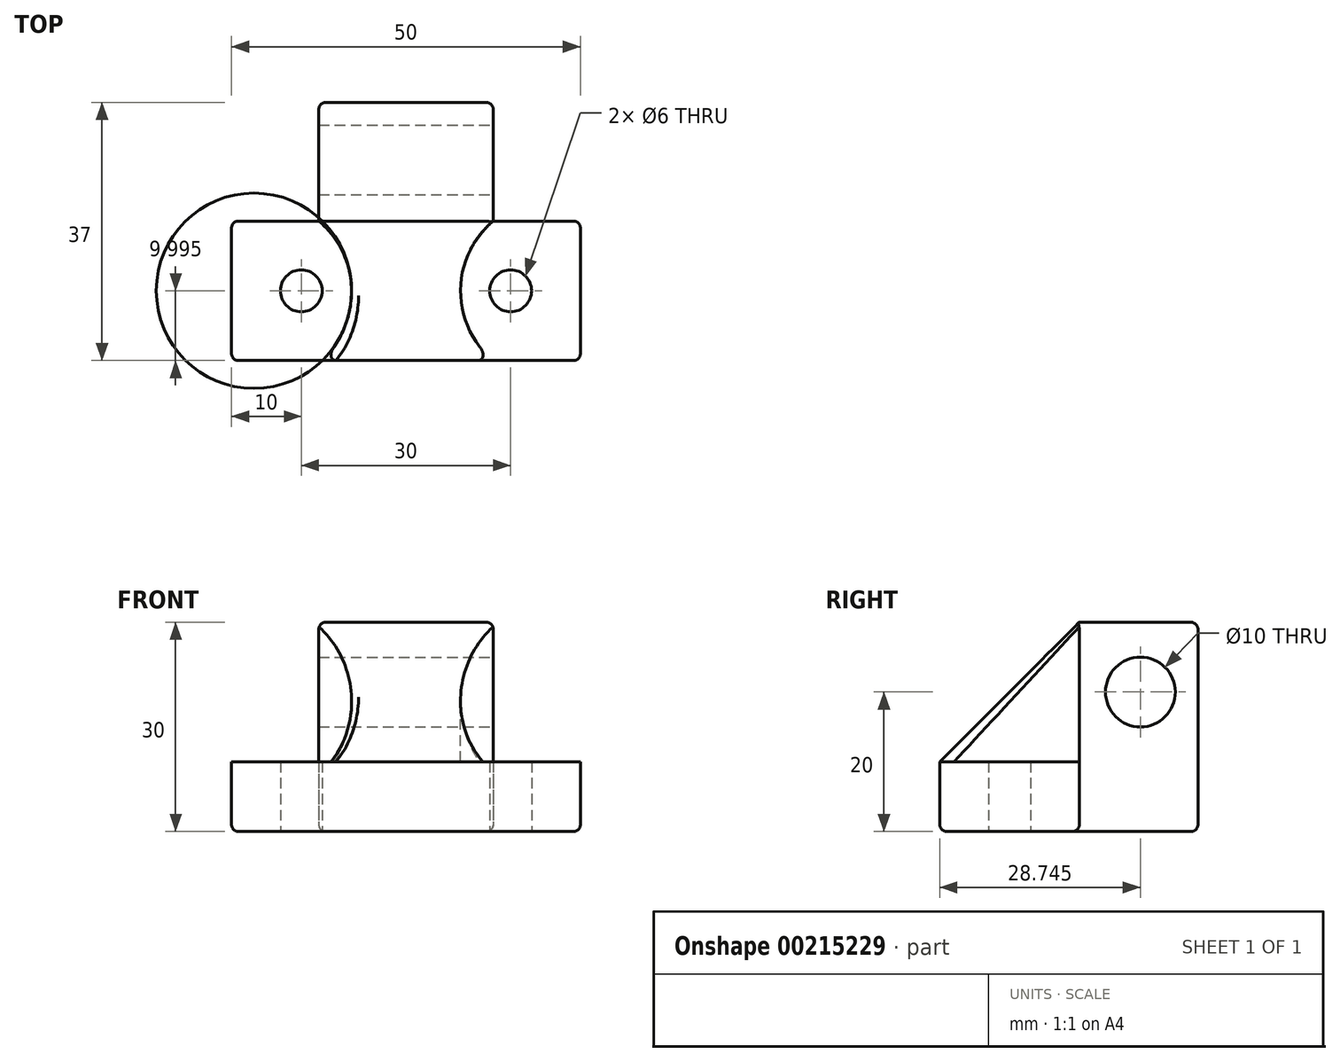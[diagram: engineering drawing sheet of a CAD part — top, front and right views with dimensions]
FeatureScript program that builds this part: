
annotation { "Feature Type Name" : "Feature", "Feature Type Description" : "" }
export const myFeature = defineFeature(function(context is Context, id is Id, definition is map)
    precondition{}
    {
        {
            var Q0;
            Q0=qCreatedBy(makeId("Top.planeOp"),FACE);
            var sketch = newSketch(context, id + "F0", { "sketchPlane" : qUnion([Q0])});
            skLineSegment(sketch, "E0.bottom", {"start": v(-9.5, 23.5) * mm, "end": v(15.5, 23.5) * mm});
            skLineSegment(sketch, "E0.top", {"start": v(-22, -13.5) * mm, "end": v(28, -13.5) * mm});
            skLineSegment(sketch, "E0.left", {"start": v(-22, 6.5) * mm, "end": v(-22, -13.5) * mm});
            skLineSegment(sketch, "E0.right", {"start": v(28, 6.5) * mm, "end": v(28, -13.5) * mm});
            skLineSegment(sketch, "E1", {"start": v(-9.5, 6.5) * mm, "end": v(-9.5, 23.5) * mm, "construction": true});
            skLineSegment(sketch, "E2", {"start": v(15.5, 23.5) * mm, "end": v(15.5, 6.5) * mm, "construction": true});
            skLineSegment(sketch, "E3", {"start": v(15.5, 23.5) * mm, "end": v(15.5, 6.5) * mm});
            skLineSegment(sketch, "E4", {"start": v(15.5, 6.5) * mm, "end": v(28, 6.5) * mm});
            skLineSegment(sketch, "E5", {"start": v(-9.5, 23.5) * mm, "end": v(-9.5, 6.5) * mm});
            skLineSegment(sketch, "E6.trimOffspring", {"start": v(15.5, 6.5) * mm, "end": v(28, 6.5) * mm, "construction": true});
            skLineSegment(sketch, "E7", {"start": v(3, 23.5) * mm, "end": v(3, -13.5) * mm, "construction": true});
            skPoint(sketch, "E8.trimOffspring.end.orphan", {"position": v(23, 23.5) * mm});
            skLineSegment(sketch, "E9", {"start": v(-22, -3.5) * mm, "end": v(28, -3.5) * mm, "construction": true});
            skLineSegment(sketch, "E10", {"start": v(18, -13.5) * mm, "end": v(18, 6.5) * mm, "construction": true});
            skLineSegment(sketch, "E11", {"start": v(18, 6.5) * mm, "end": v(15.5, 6.5) * mm});
            skLineSegment(sketch, "E12", {"start": v(-22, 6.5) * mm, "end": v(-9.5, 6.5) * mm});
            skLineSegment(sketch, "E13", {"start": v(-12, 6.5) * mm, "end": v(-12, -13.5) * mm, "construction": true});
            skCircle(sketch, "E14", {"center": v(-12, -3.5) * mm, "radius": 3 * mm});
            skCircle(sketch, "E15", {"center": v(18, -3.5) * mm, "radius": 3 * mm});
            skSolve(sketch);
        }
        {
            var Q0;
            Q0=makeQuery(id+"F0.imprint","IMPRINT",FACE,{"disambiguationData":[TD([[makeQuery(id+"F0.imprint","IMPRINT",EDGE,{"derivedFrom":sQuery(id+"F0.wireOp",EDGE,"E0.bottom")}),-1.0]])]});
            extrude(context, id + "F1", {"entities" : qUnion([Q0]), "depth" : 30 * mm});
        }
        {
            var Q0;
            Q0=makeQuery(id+"F1.opExtrude","CAP_FACE",FACE,{"disambiguationData":[OSD([sQuery(id+"F0.wireOp",EDGE,"E0.bottom"),sQuery(id+"F0.wireOp",EDGE,"E0.top"),sQuery(id+"F0.wireOp",EDGE,"E0.left"),sQuery(id+"F0.wireOp",EDGE,"E0.right"),sQuery(id+"F0.wireOp",EDGE,"E3"),sQuery(id+"F0.wireOp",EDGE,"E4"),sQuery(id+"F0.wireOp",EDGE,"E5"),sQuery(id+"F0.wireOp",EDGE,"E11"),sQuery(id+"F0.wireOp",EDGE,"E12"),sQuery(id+"F0.wireOp",EDGE,"E14"),sQuery(id+"F0.wireOp",EDGE,"E15")])],"isStart":false});
            var sketch = newSketch(context, id + "F2", { "sketchPlane" : qUnion([Q0])});
            skLineSegment(sketch, "E16.bottom", {"start": v(15.5, 6.5) * mm, "end": v(28, 6.5) * mm});
            skLineSegment(sketch, "E16.right", {"start": v(28, 6.5) * mm, "end": v(28, -13.5) * mm});
            skLineSegment(sketch, "E17.bottom", {"start": v(-22, 6.5) * mm, "end": v(-9.5, 6.5) * mm});
            skLineSegment(sketch, "E17.left", {"start": v(-22, 6.5) * mm, "end": v(-22, -13.5) * mm});
            skArc(sketch, "E18", {"start": v(-4.8, -3.5) * mm, "mid": v(-6.03, 2.02) * mm, "end": v(-9.5, 6.5) * mm});
            skArc(sketch, "E19", {"start": v(-9, -13.5) * mm, "mid": v(-5.89, -8.93) * mm, "end": v(-4.8, -3.5) * mm});
            skArc(sketch, "E20", {"start": v(15.5, 6.5) * mm, "mid": v(12.04, 2.02) * mm, "end": v(10.8, -3.5) * mm});
            skArc(sketch, "E21", {"start": v(10.8, -3.5) * mm, "mid": v(12.04, -9.03) * mm, "end": v(15.5, -13.5) * mm});
            skPoint(sketch, "E22.trimOffspring.end.orphan", {"position": v(28, -3.5) * mm});
            skPoint(sketch, "E23.start.orphan", {"position": v(-22, -3.5) * mm});
            skSolve(sketch);
        }
        {
            var Q0;
            Q0=makeQuery(id+"F2.imprint","IMPRINT",FACE,{"disambiguationData":[TD([[makeQuery(id+"F2.imprint","IMPRINT",EDGE,{"derivedFrom":sQuery(id+"F2.wireOp",EDGE,"E17.bottom")}),-1.0]])]});
            var Q1;
            Q1=makeQuery(id+"F2.imprint","IMPRINT",FACE,{"disambiguationData":[TD([[makeQuery(id+"F2.imprint","IMPRINT",EDGE,{"derivedFrom":sQuery(id+"F2.wireOp",EDGE,"E16.bottom")}),-1.0]])]});
            extrude(context, id + "F3", {"entities" : qUnion([Q0, Q1]), "operationType" : NewBodyOperationType.REMOVE, "oppositeDirection" : true, "depth" : 20 * mm});
        }
        {
            var Q0;
            Q0=makeQuery(id+"F1.opExtrude","SWEPT_FACE",FACE,{"disambiguationData":[OSD([sQuery(id+"F0.wireOp",EDGE,"E0.right")])]});
            var sketch = newSketch(context, id + "F4", { "sketchPlane" : qUnion([Q0])});
            skLineSegment(sketch, "E24.top", {"start": v(-13.5, 30) * mm, "end": v(6.5, 30) * mm});
            skLineSegment(sketch, "E24.left", {"start": v(-13.5, 10) * mm, "end": v(-13.5, 30) * mm});
            skLineSegment(sketch, "E25", {"start": v(-13.5, 10) * mm, "end": v(6.5, 30) * mm});
            skSolve(sketch);
        }
        {
            var Q0;
            Q0=makeQuery(id+"F4.imprint","IMPRINT",FACE,{"disambiguationData":[TD([[makeQuery(id+"F4.imprint","IMPRINT",EDGE,{"derivedFrom":sQuery(id+"F4.wireOp",EDGE,"E24.top")}),-1.0]])]});
            extrude(context, id + "F5", {"entities" : qUnion([Q0]), "operationType" : NewBodyOperationType.REMOVE, "oppositeDirection" : true, "depth" : 50 * mm});
        }
        {
            var Q0;
            Q0=makeQuery(id+"F1.opExtrude","SWEPT_FACE",FACE,{"disambiguationData":[OSD([sQuery(id+"F0.wireOp",EDGE,"E3")])]});
            var sketch = newSketch(context, id + "F6", { "sketchPlane" : qUnion([Q0])});
            skCircle(sketch, "E26", {"center": v(15.25, 20) * mm, "radius": 5 * mm});
            skPoint(sketch, "E27.trimOffspring.end.orphan", {"position": v(13.5, 0) * mm});
            skPoint(sketch, "E28.orphan", {"position": v(6.5, 20) * mm});
            skSolve(sketch);
        }
        {
            var Q0;
            Q0=makeQuery(id+"F6.imprint","IMPRINT",FACE,{"disambiguationData":[TD([[makeQuery(id+"F6.imprint","IMPRINT",EDGE,{"derivedFrom":sQuery(id+"F6.wireOp",EDGE,"E26")}),1.0]])]});
            extrude(context, id + "F7", {"entities" : qUnion([Q0]), "operationType" : NewBodyOperationType.REMOVE, "oppositeDirection" : true, "depth" : 25 * mm});
        }
        {
            var Q0;
            Q0=makeQuery(id+"F1.opExtrude","CAP_EDGE",EDGE,{"disambiguationData":[OSD([sQuery(id+"F0.wireOp",EDGE,"E0.bottom")])],"isStart":false});
            var Q1;
            Q1=makeQuery(id+"F1.opExtrude","CAP_EDGE",EDGE,{"disambiguationData":[OSD([sQuery(id+"F0.wireOp",EDGE,"E3")])],"isStart":false});
            var Q2;
            Q2=makeQuery(id+"F1.opExtrude","CAP_EDGE",EDGE,{"disambiguationData":[OSD([sQuery(id+"F0.wireOp",EDGE,"E5")])],"isStart":false});
            var Q3;
            Q3=makeQuery(id+"F3.boolean.opBoolean","COPY",EDGE,{"derivedFrom":makeQuery(id+"F3.opExtrude","CAP_EDGE",EDGE,{"disambiguationData":[OSD([sQuery(id+"F2.wireOp",EDGE,"E16.right")])],"isStart":false})});
            var Q4;
            Q4=makeQuery(id+"F3.boolean.opBoolean","COPY",EDGE,{"derivedFrom":makeQuery(id+"F3.opExtrude","CAP_EDGE",EDGE,{"disambiguationData":[OSD([sQuery(id+"F2.wireOp",EDGE,"E16.bottom")])],"isStart":false})});
            var Q5;
            {var subQ0=sQuery(id+"F0.wireOp",EDGE,"E0.top");var subQ1=makeQuery(id+"F1.opExtrude","CAP_EDGE",EDGE,{"disambiguationData":[OSD([subQ0])],"isStart":false});Q5=makeQuery(id+"F3.boolean.opBoolean","COPY",EDGE,{"derivedFrom":makeQuery(id+"F3.opExtrude","CAP_EDGE",EDGE,{"disambiguationData":[OSD([subQ0]),TDD([makeQuery(id+"F2.imprint","IMPRINT",EDGE,{"disambiguationData":[TD([[makeQuery(id+"F2.imprint","INTERSECT",VERTEX,{"derivedFrom":[subQ1,sQuery(id+"F2.wireOp",EDGE,"E16.right")]}),1.0]])],"derivedFrom":subQ1})])],"isStart":false})});}
            var Q6;
            Q6=makeQuery(id+"F1.opExtrude","SWEPT_EDGE",EDGE,{"disambiguationData":[OSD([sQuery(id+"F0.wireOp",EDGE,"E0.top"),sQuery(id+"F0.wireOp",EDGE,"E0.right")])]});
            var Q7;
            Q7=makeQuery(id+"F1.opExtrude","CAP_EDGE",EDGE,{"disambiguationData":[OSD([sQuery(id+"F0.wireOp",EDGE,"E0.right")])],"isStart":true});
            var Q8;
            Q8=makeQuery(id+"F1.opExtrude","SWEPT_EDGE",EDGE,{"disambiguationData":[OSD([sQuery(id+"F0.wireOp",EDGE,"E0.right"),sQuery(id+"F0.wireOp",EDGE,"E4")])]});
            var Q9;
            Q9=makeQuery(id+"F1.opExtrude","CAP_EDGE",EDGE,{"disambiguationData":[OSD([sQuery(id+"F0.wireOp",EDGE,"E3")])],"isStart":true});
            var Q10;
            Q10=makeQuery(id+"F1.opExtrude","SWEPT_EDGE",EDGE,{"disambiguationData":[OSD([sQuery(id+"F0.wireOp",EDGE,"E0.bottom"),sQuery(id+"F0.wireOp",EDGE,"E3")])]});
            var Q11;
            Q11=makeQuery(id+"F1.opExtrude","CAP_EDGE",EDGE,{"disambiguationData":[OSD([sQuery(id+"F0.wireOp",EDGE,"E0.bottom")])],"isStart":true});
            var Q12;
            Q12=makeQuery(id+"F1.opExtrude","CAP_EDGE",EDGE,{"disambiguationData":[OSD([sQuery(id+"F0.wireOp",EDGE,"E4"),sQuery(id+"F0.wireOp",EDGE,"E11")])],"isStart":true});
            var Q13;
            Q13=makeQuery(id+"F1.opExtrude","SWEPT_EDGE",EDGE,{"disambiguationData":[OSD([sQuery(id+"F0.wireOp",EDGE,"E0.bottom"),sQuery(id+"F0.wireOp",EDGE,"E5")])]});
            var Q14;
            Q14=makeQuery(id+"F1.opExtrude","CAP_EDGE",EDGE,{"disambiguationData":[OSD([sQuery(id+"F0.wireOp",EDGE,"E5")])],"isStart":true});
            var Q15;
            Q15=makeQuery(id+"F1.opExtrude","CAP_EDGE",EDGE,{"disambiguationData":[OSD([sQuery(id+"F0.wireOp",EDGE,"E12")])],"isStart":true});
            var Q16;
            Q16=makeQuery(id+"F1.opExtrude","CAP_EDGE",EDGE,{"disambiguationData":[OSD([sQuery(id+"F0.wireOp",EDGE,"E0.top")])],"isStart":true});
            var Q17;
            Q17=makeQuery(id+"F1.opExtrude","CAP_EDGE",EDGE,{"disambiguationData":[OSD([sQuery(id+"F0.wireOp",EDGE,"E0.left")])],"isStart":true});
            var Q18;
            Q18=makeQuery(id+"F1.opExtrude","SWEPT_EDGE",EDGE,{"disambiguationData":[OSD([sQuery(id+"F0.wireOp",EDGE,"E0.left"),sQuery(id+"F0.wireOp",EDGE,"E12")])]});
            var Q19;
            Q19=makeQuery(id+"F3.boolean.opBoolean","COPY",EDGE,{"derivedFrom":makeQuery(id+"F3.opExtrude","CAP_EDGE",EDGE,{"disambiguationData":[OSD([sQuery(id+"F2.wireOp",EDGE,"E17.bottom")])],"isStart":false})});
            var Q20;
            Q20=makeQuery(id+"F1.opExtrude","SWEPT_EDGE",EDGE,{"disambiguationData":[OSD([sQuery(id+"F0.wireOp",EDGE,"E0.top"),sQuery(id+"F0.wireOp",EDGE,"E0.left")])]});
            var Q21;
            Q21=makeQuery(id+"F3.boolean.opBoolean","COPY",EDGE,{"derivedFrom":makeQuery(id+"F3.opExtrude","CAP_EDGE",EDGE,{"disambiguationData":[OSD([sQuery(id+"F2.wireOp",EDGE,"E17.left")])],"isStart":false})});
            var Q22;
            {var subQ0=sQuery(id+"F0.wireOp",EDGE,"E0.top");var subQ1=makeQuery(id+"F1.opExtrude","CAP_EDGE",EDGE,{"disambiguationData":[OSD([subQ0])],"isStart":false});Q22=makeQuery(id+"F3.boolean.opBoolean","COPY",EDGE,{"derivedFrom":makeQuery(id+"F3.opExtrude","CAP_EDGE",EDGE,{"disambiguationData":[OSD([subQ0]),TDD([makeQuery(id+"F2.imprint","IMPRINT",EDGE,{"disambiguationData":[TD([[makeQuery(id+"F2.imprint","INTERSECT",VERTEX,{"derivedFrom":[subQ1,sQuery(id+"F2.wireOp",EDGE,"E17.left")]}),-1.0]])],"derivedFrom":subQ1})])],"isStart":false})});}
            fillet(context, id + "F8", {"entities" : qUnion([Q0, Q1, Q2, Q3, Q4, Q5, Q6, Q7, Q8, Q9, Q10, Q11, Q12, Q13, Q14, Q15, Q16, Q17, Q18, Q19, Q20, Q21, Q22]), "radius" : 1 * mm, "tangentPropagation" : true, "allowEdgeOverflow" : false});
        }
        {
            var Q0;
            Q0=makeQuery(id+"F5.boolean.opBoolean","COPY",EDGE,{"derivedFrom":makeQuery(id+"F5.opExtrude","SWEPT_EDGE",EDGE,{"disambiguationData":[OSD([sQuery(id+"F0.wireOp",EDGE,"E0.top"),sQuery(id+"F0.wireOp",EDGE,"E0.right"),sQuery(id+"F2.wireOp",EDGE,"E16.right"),sQuery(id+"F4.wireOp",EDGE,"E24.left"),sQuery(id+"F4.wireOp",EDGE,"E25")])]})});
            var Q1;
            Q1=makeQuery(id+"F5.boolean.opBoolean","INTERSECT",EDGE,{"derivedFrom":[makeQuery(id+"F3.boolean.opBoolean","COPY",FACE,{"derivedFrom":makeQuery(id+"F3.opExtrude","SWEPT_FACE",FACE,{"disambiguationData":[OSD([sQuery(id+"F2.wireOp",EDGE,"E18")])]})}),makeQuery(id+"F5.opExtrude","SWEPT_FACE",FACE,{"disambiguationData":[OSD([sQuery(id+"F4.wireOp",EDGE,"E25")])]})]});
            var Q2;
            Q2=makeQuery(id+"F5.boolean.opBoolean","INTERSECT",EDGE,{"derivedFrom":[makeQuery(id+"F3.boolean.opBoolean","COPY",FACE,{"derivedFrom":makeQuery(id+"F3.opExtrude","SWEPT_FACE",FACE,{"disambiguationData":[OSD([sQuery(id+"F2.wireOp",EDGE,"E19")])]})}),makeQuery(id+"F5.opExtrude","SWEPT_FACE",FACE,{"disambiguationData":[OSD([sQuery(id+"F4.wireOp",EDGE,"E25")])]})]});
            var Q3;
            Q3=makeQuery(id+"F5.boolean.opBoolean","INTERSECT",EDGE,{"derivedFrom":[makeQuery(id+"F3.boolean.opBoolean","COPY",FACE,{"derivedFrom":makeQuery(id+"F3.opExtrude","SWEPT_FACE",FACE,{"disambiguationData":[OSD([sQuery(id+"F2.wireOp",EDGE,"E20"),sQuery(id+"F2.wireOp",EDGE,"E21")])]})}),makeQuery(id+"F5.opExtrude","SWEPT_FACE",FACE,{"disambiguationData":[OSD([sQuery(id+"F4.wireOp",EDGE,"E25")])]})]});
            fillet(context, id + "F9", {"entities" : qUnion([Q0, Q1, Q2, Q3]), "radius" : 1 * mm, "tangentPropagation" : true, "allowEdgeOverflow" : false});
        }
    });
